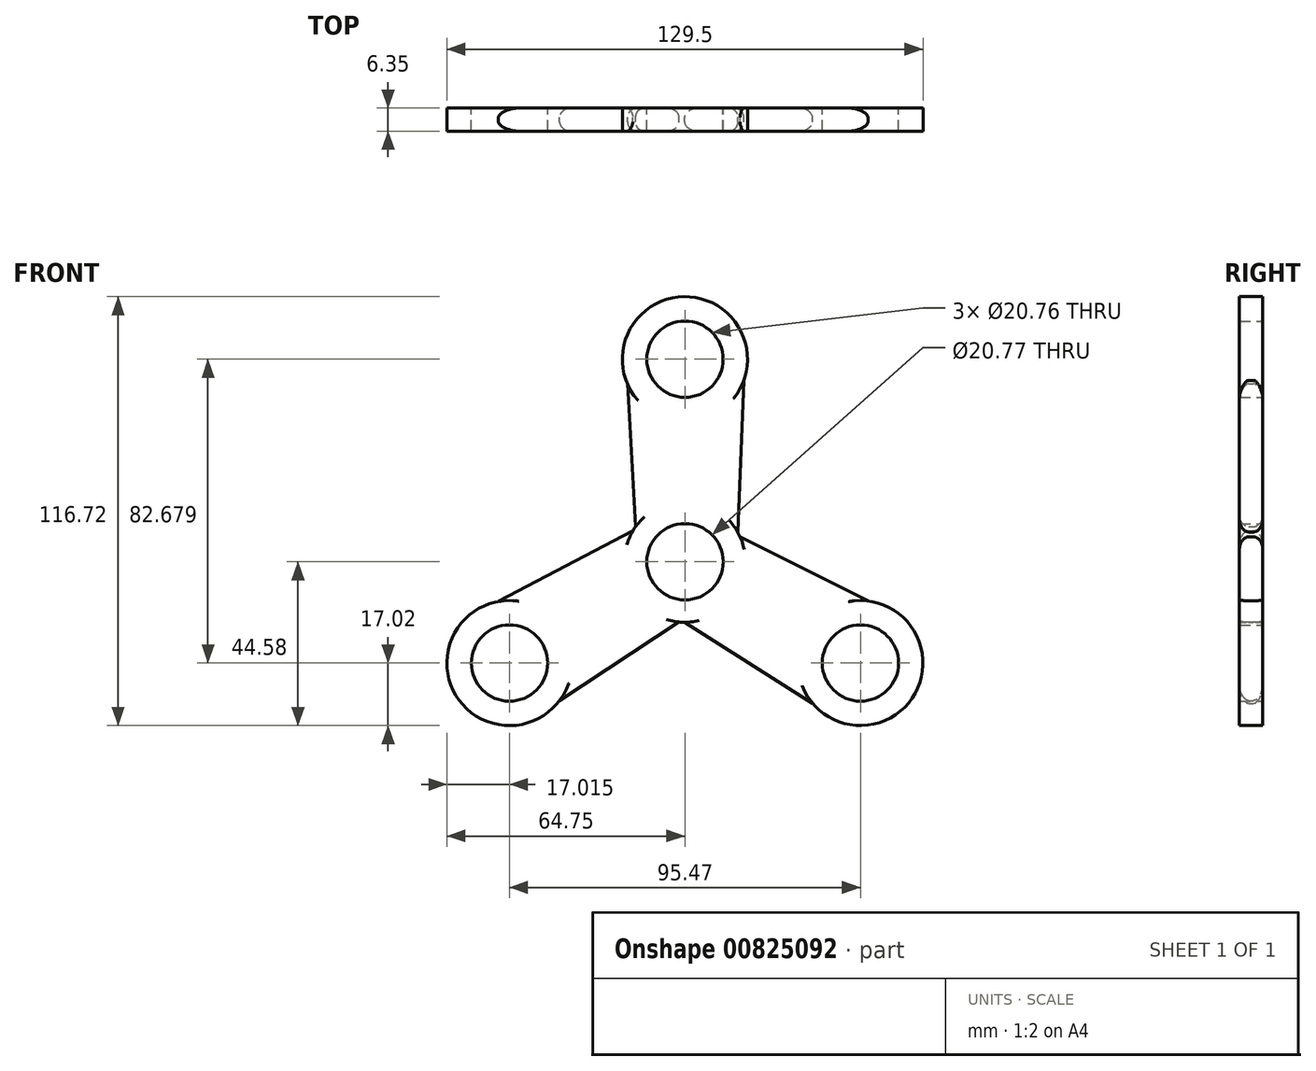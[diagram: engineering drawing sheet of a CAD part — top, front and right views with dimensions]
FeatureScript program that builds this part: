
annotation { "Feature Type Name" : "Feature", "Feature Type Description" : "" }
export const myFeature = defineFeature(function(context is Context, id is Id, definition is map)
    precondition{}
    {
        {
            var Q0;
            Q0=qCreatedBy(makeId("Front.planeOp"),FACE);
            var sketch = newSketch(context, id + "F0", { "sketchPlane" : qUnion([Q0])});
            skCircle(sketch, "E0", {"center": v(0, 0) * mm, "radius": 10.39 * mm});
            skCircle(sketch, "E1", {"center": v(0, 55.12) * mm, "radius": 10.38 * mm});
            skArc(sketch, "E2", {"start": v(16, 49.33) * mm, "mid": v(-0.49, 72.13) * mm, "end": v(-15.65, 48.43) * mm});
            skArc(sketch, "E3", {"start": v(-13.4, 9.58) * mm, "mid": v(-0.88, -16.44) * mm, "end": v(14.33, 8.1) * mm});
            skLineSegment(sketch, "E4", {"start": v(16, 49.33) * mm, "end": v(14.33, 8.1) * mm});
            skLineSegment(sketch, "E5", {"start": v(-13.4, 9.58) * mm, "end": v(-15.65, 48.43) * mm});
            skCircle(sketch, "E6.1.0", {"center": v(-47.73, -27.56) * mm, "radius": 10.38 * mm});
            skLineSegment(sketch, "E6.1.1", {"start": v(-50.72, -10.8) * mm, "end": v(-14.18, 8.36) * mm});
            skLineSegment(sketch, "E6.1.2", {"start": v(-1.6, -16.38) * mm, "end": v(-34.12, -37.77) * mm});
            skArc(sketch, "E6.1.3", {"start": v(-50.72, -10.8) * mm, "mid": v(-62.22, -36.49) * mm, "end": v(-34.12, -37.77) * mm});
            skCircle(sketch, "E6.2.0", {"center": v(47.73, -27.56) * mm, "radius": 10.38 * mm});
            skLineSegment(sketch, "E6.2.1", {"start": v(34.72, -38.53) * mm, "end": v(-0.15, -16.46) * mm});
            skLineSegment(sketch, "E6.2.2", {"start": v(14.99, 6.8) * mm, "end": v(49.76, -10.66) * mm});
            skArc(sketch, "E6.2.3", {"start": v(34.72, -38.53) * mm, "mid": v(62.7, -35.65) * mm, "end": v(49.76, -10.66) * mm});
            skSolve(sketch);
        }
        {
            var Q0;
            Q0 = qSketchRegion(id + "F0", true);
            extrude(context, id + "F1", {"entities" : qUnion([Q0]), "depth" : 6.35 * mm, "offsetDistance" : 25.4 * mm});
        }
        {
            var Q0;
            Q0=makeQuery(id+"F1.opExtrude","CAP_EDGE",EDGE,{"disambiguationData":[OSD([sQuery(id+"F0.wireOp",EDGE,"E4")])],"isStart":true});
            var Q1;
            Q1=makeQuery(id+"F1.opExtrude","CAP_EDGE",EDGE,{"disambiguationData":[OSD([sQuery(id+"F0.wireOp",EDGE,"E5")])],"isStart":true});
            var Q2;
            Q2=makeQuery(id+"F1.opExtrude","CAP_EDGE",EDGE,{"disambiguationData":[OSD([sQuery(id+"F0.wireOp",EDGE,"E6.2.2")])],"isStart":true});
            var Q3;
            Q3=makeQuery(id+"F1.opExtrude","CAP_EDGE",EDGE,{"disambiguationData":[OSD([sQuery(id+"F0.wireOp",EDGE,"E6.2.1")])],"isStart":true});
            var Q4;
            Q4=makeQuery(id+"F1.opExtrude","CAP_EDGE",EDGE,{"disambiguationData":[OSD([sQuery(id+"F0.wireOp",EDGE,"E6.1.2")])],"isStart":true});
            var Q5;
            Q5=makeQuery(id+"F1.opExtrude","CAP_EDGE",EDGE,{"disambiguationData":[OSD([sQuery(id+"F0.wireOp",EDGE,"E6.1.1")])],"isStart":true});
            fillet(context, id + "F2", {"entities" : qUnion([Q0, Q1, Q2, Q3, Q4, Q5]), "radius" : 2.54 * mm, "tangentPropagation" : true, "allowEdgeOverflow" : false});
        }
        {
            var Q0;
            Q0=makeQuery(id+"F1.opExtrude","CAP_EDGE",EDGE,{"disambiguationData":[OSD([sQuery(id+"F0.wireOp",EDGE,"E4")])],"isStart":false});
            var Q1;
            Q1=makeQuery(id+"F1.opExtrude","CAP_EDGE",EDGE,{"disambiguationData":[OSD([sQuery(id+"F0.wireOp",EDGE,"E5")])],"isStart":false});
            var Q2;
            Q2=makeQuery(id+"F1.opExtrude","CAP_EDGE",EDGE,{"disambiguationData":[OSD([sQuery(id+"F0.wireOp",EDGE,"E6.1.1")])],"isStart":false});
            var Q3;
            Q3=makeQuery(id+"F1.opExtrude","CAP_EDGE",EDGE,{"disambiguationData":[OSD([sQuery(id+"F0.wireOp",EDGE,"E6.1.2")])],"isStart":false});
            var Q4;
            Q4=makeQuery(id+"F1.opExtrude","CAP_EDGE",EDGE,{"disambiguationData":[OSD([sQuery(id+"F0.wireOp",EDGE,"E6.2.1")])],"isStart":false});
            var Q5;
            Q5=makeQuery(id+"F1.opExtrude","CAP_EDGE",EDGE,{"disambiguationData":[OSD([sQuery(id+"F0.wireOp",EDGE,"E6.2.2")])],"isStart":false});
            fillet(context, id + "F3", {"entities" : qUnion([Q0, Q1, Q2, Q3, Q4, Q5]), "radius" : 2.54 * mm, "tangentPropagation" : true, "allowEdgeOverflow" : false});
        }
    });
